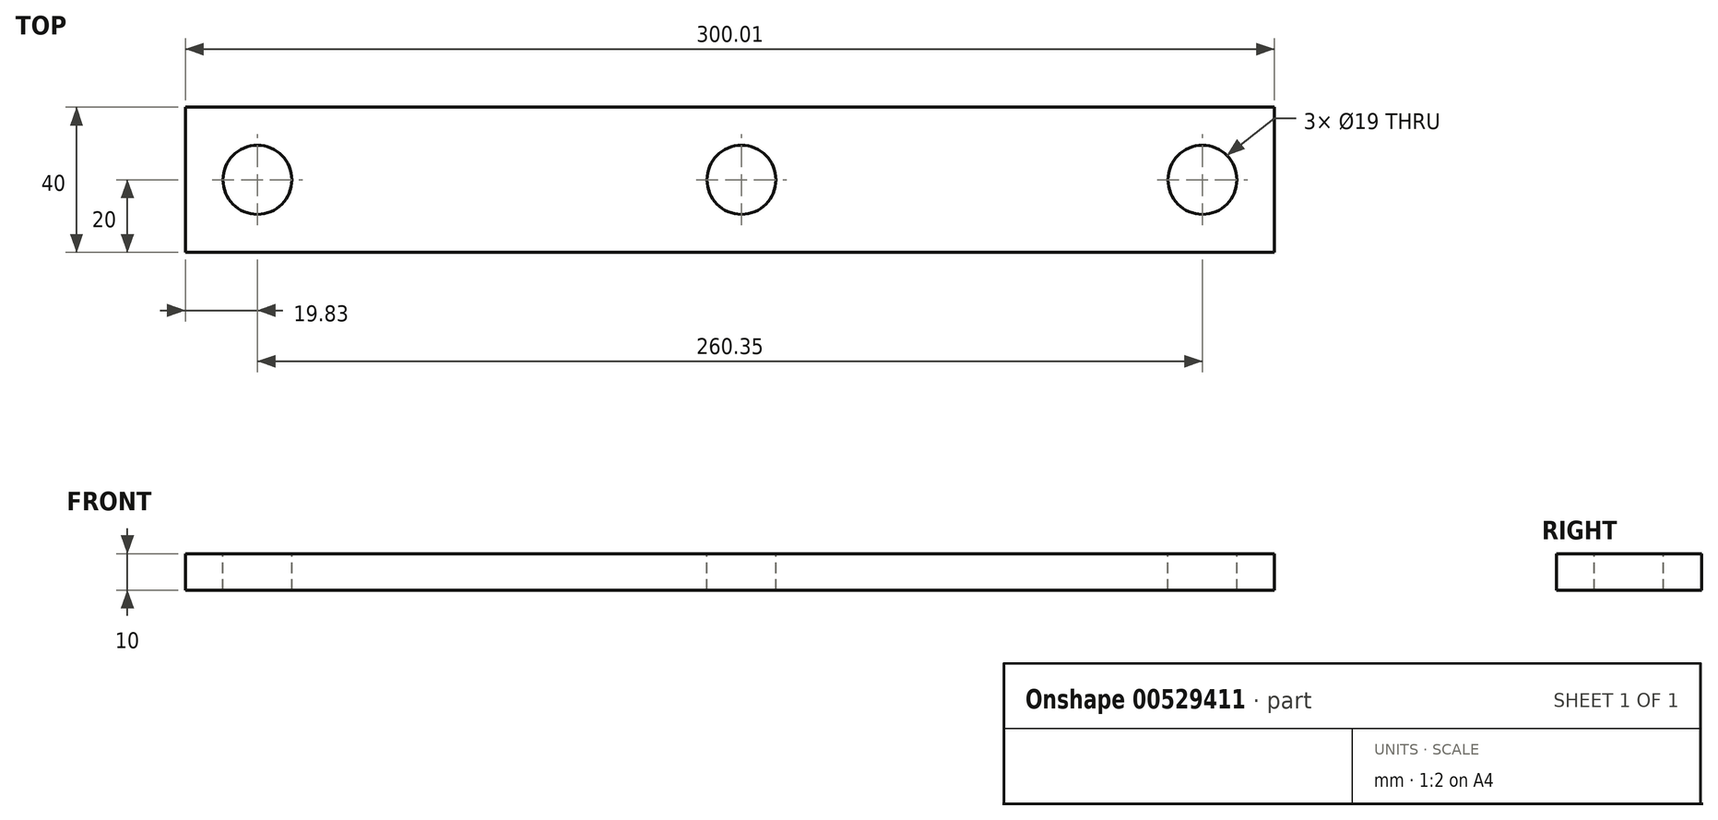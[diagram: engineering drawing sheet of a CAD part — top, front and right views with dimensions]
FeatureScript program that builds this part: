
annotation { "Feature Type Name" : "Feature", "Feature Type Description" : "" }
export const myFeature = defineFeature(function(context is Context, id is Id, definition is map)
    precondition{}
    {
        {
            var Q0;
            Q0=qCreatedBy(makeId("Top.planeOp"),FACE);
            var sketch = newSketch(context, id + "F0", { "sketchPlane" : qUnion([Q0])});
            skPoint(sketch, "E0.middle", {"position": v(0, 0) * mm});
            skLineSegment(sketch, "E1", {"start": v(0, 0) * mm, "end": v(-133.35, 0) * mm, "construction": true});
            skLineSegment(sketch, "E2", {"start": v(0, 0) * mm, "end": v(127, 0) * mm, "construction": true});
            skCircle(sketch, "E3", {"center": v(-133.35, 0) * mm, "radius": 9.5 * mm});
            skCircle(sketch, "E4", {"center": v(0, 0) * mm, "radius": 9.5 * mm});
            skCircle(sketch, "E5", {"center": v(127, 0) * mm, "radius": 9.5 * mm});
            skLineSegment(sketch, "E6", {"start": v(0, 0) * mm, "end": v(0, -20) * mm, "construction": true});
            skLineSegment(sketch, "E7", {"start": v(127, 0) * mm, "end": v(146.82, 0) * mm, "construction": true});
            skLineSegment(sketch, "E8", {"start": v(-133.35, 0) * mm, "end": v(-153.18, 0) * mm, "construction": true});
            skLineSegment(sketch, "E9", {"start": v(0, -20) * mm, "end": v(-153.18, -20) * mm});
            skLineSegment(sketch, "E10.MirrorCS", {"start": v(0, 20) * mm, "end": v(-153.18, 20) * mm});
            skLineSegment(sketch, "E11", {"start": v(0, -20) * mm, "end": v(146.82, -20) * mm});
            skLineSegment(sketch, "E12.MirrorCS", {"start": v(0, 20) * mm, "end": v(146.82, 20) * mm});
            skLineSegment(sketch, "E13", {"start": v(146.82, 20) * mm, "end": v(146.82, -20) * mm});
            skLineSegment(sketch, "E14", {"start": v(-153.18, 20) * mm, "end": v(-153.18, -20) * mm});
            skSolve(sketch);
        }
        {
            var Q0;
            Q0=makeQuery(id+"F0.imprint","IMPRINT",FACE,{"disambiguationData":[TD([[makeQuery(id+"F0.imprint","IMPRINT",EDGE,{"derivedFrom":sQuery(id+"F0.wireOp",EDGE,"E3")}),-1.0]])]});
            extrude(context, id + "F1", {"entities" : qUnion([Q0]), "oppositeDirection" : true, "depth" : 10 * mm, "offsetDistance" : 25 * mm});
        }
    });
